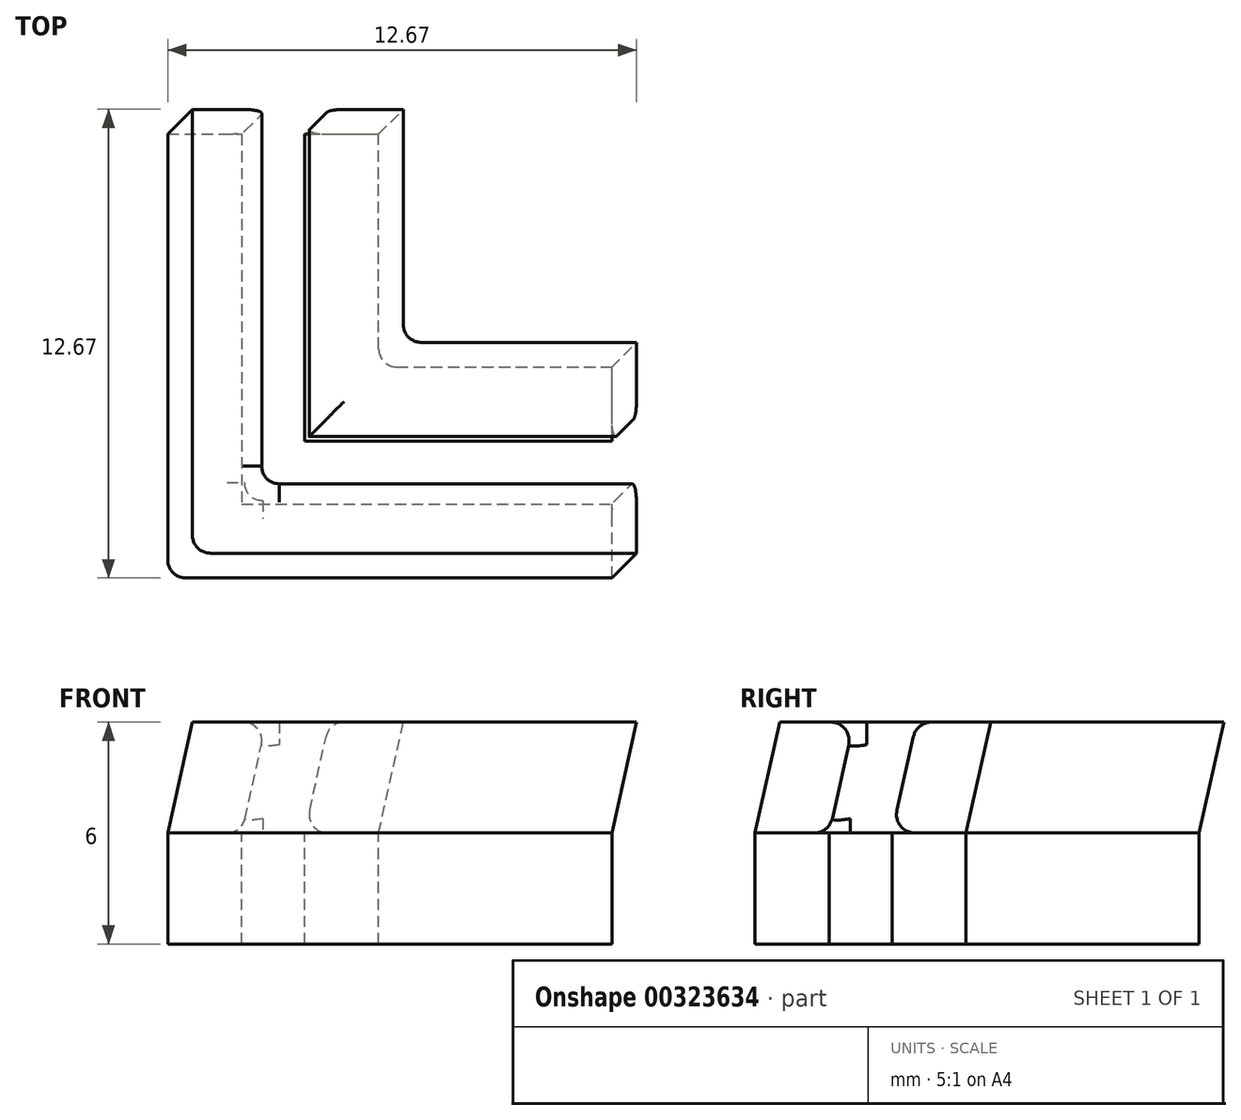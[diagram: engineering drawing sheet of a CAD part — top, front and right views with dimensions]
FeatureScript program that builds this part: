
annotation { "Feature Type Name" : "Feature", "Feature Type Description" : "" }
export const myFeature = defineFeature(function(context is Context, id is Id, definition is map)
    precondition{}
    {
        {
            assignVariable(context, id + "F0", {"name" : "H", "anyValue" : 3});
        }
        {
            var Q0;
            Q0=qCreatedBy(makeId("Top.planeOp"),FACE);
            var sketch = newSketch(context, id + "F1", { "sketchPlane" : qUnion([Q0])});
            skLineSegment(sketch, "E0.bottom", {"start": v(0, 0) * mm, "end": v(12, 0) * mm});
            skLineSegment(sketch, "E0.left", {"start": v(0, 0) * mm, "end": v(0, 12) * mm});
            skLineSegment(sketch, "E0.right", {"start": v(12, 0) * mm, "end": v(12, 5.7) * mm});
            skLineSegment(sketch, "E1.top", {"start": v(0, 12) * mm, "end": v(5.7, 12) * mm});
            skLineSegment(sketch, "E2.bottom", {"start": v(2, 12) * mm, "end": v(3.7, 12) * mm});
            skLineSegment(sketch, "E2.left", {"start": v(2, 12) * mm, "end": v(2, 2) * mm});
            skLineSegment(sketch, "E2.right", {"start": v(3.7, 12) * mm, "end": v(3.7, 3.7) * mm});
            skLineSegment(sketch, "E3.bottom", {"start": v(3.7, 3.7) * mm, "end": v(12, 3.7) * mm});
            skLineSegment(sketch, "E3.top", {"start": v(2, 2) * mm, "end": v(12, 2) * mm});
            skLineSegment(sketch, "E3.right", {"start": v(12, 3.7) * mm, "end": v(12, 2) * mm});
            skLineSegment(sketch, "E4.trimOffspring", {"start": v(5.7, 5.7) * mm, "end": v(12, 5.7) * mm});
            skLineSegment(sketch, "E5.trimOffspring", {"start": v(5.7, 5.7) * mm, "end": v(5.7, 12) * mm});
            skSolve(sketch);
        }
        {
            var Q0;
            {var subQ4=sQuery(id+"F1.wireOp",EDGE,"E0.bottom");Q0=makeQuery(id+"F1.imprint","IMPRINT",FACE,{"disambiguationData":[TD([[makeQuery(id+"F1.imprint","IMPRINT",EDGE,{"derivedFrom":subQ4}),1.0]])]});}
            cPlane(context, id + "F2", {"entities" : qUnion([Q0]), "cplaneType" : CPlaneType.OFFSET, "offset" : (getVariable(context, 'H')) * mm, "width" : 150 * mm, "height" : 150 * mm});
        }
        {
            var Q0;
            Q0=qCreatedBy(id+"F2.planeOp",FACE);
            var sketch = newSketch(context, id + "F3", { "sketchPlane" : qUnion([Q0])});
            skLineSegment(sketch, "E6.bottom", {"start": v(0.67, 0.67) * mm, "end": v(12.67, 0.67) * mm});
            skLineSegment(sketch, "E6.left", {"start": v(0.67, 0.67) * mm, "end": v(0.67, 12.67) * mm});
            skLineSegment(sketch, "E6.right", {"start": v(12.67, 0.67) * mm, "end": v(12.67, 6.37) * mm});
            skLineSegment(sketch, "E7.top", {"start": v(0.67, 12.67) * mm, "end": v(6.37, 12.67) * mm});
            skLineSegment(sketch, "E8.bottom", {"start": v(2.67, 12.67) * mm, "end": v(4.37, 12.67) * mm});
            skLineSegment(sketch, "E8.left", {"start": v(2.67, 12.67) * mm, "end": v(2.67, 2.67) * mm});
            skLineSegment(sketch, "E8.right", {"start": v(4.37, 12.67) * mm, "end": v(4.37, 4.37) * mm});
            skLineSegment(sketch, "E9.bottom", {"start": v(4.37, 4.37) * mm, "end": v(12.67, 4.37) * mm});
            skLineSegment(sketch, "E9.top", {"start": v(2.67, 2.67) * mm, "end": v(12.67, 2.67) * mm});
            skLineSegment(sketch, "E9.right", {"start": v(12.67, 4.37) * mm, "end": v(12.67, 2.67) * mm});
            skLineSegment(sketch, "E10.trimOffspring", {"start": v(6.37, 6.37) * mm, "end": v(12.67, 6.37) * mm});
            skLineSegment(sketch, "E11.trimOffspring", {"start": v(6.37, 6.37) * mm, "end": v(6.37, 12.67) * mm});
            skSolve(sketch);
        }
        {
            var Q0;
            {var subQ4=sQuery(id+"F1.wireOp",EDGE,"E0.bottom");Q0=makeQuery(id+"F1.imprint","IMPRINT",FACE,{"disambiguationData":[TD([[makeQuery(id+"F1.imprint","IMPRINT",EDGE,{"derivedFrom":subQ4}),1.0]])]});}
            var Q1;
            {var subQ4=sQuery(id+"F3.wireOp",EDGE,"E6.bottom");Q1=makeQuery(id+"F3.imprint","IMPRINT",FACE,{"disambiguationData":[TD([[makeQuery(id+"F3.imprint","IMPRINT",EDGE,{"derivedFrom":subQ4}),1.0]])]});}
            loft(context, id + "F4", {"sheetProfilesArray" : [{ "sheetProfileEntities" : qUnion([Q0]) }, { "sheetProfileEntities" : qUnion([Q1]) }]});
        }
        {
            var Q0;
            {var subQ3=sQuery(id+"F1.wireOp",EDGE,"E2.right");Q0=makeQuery(id+"F1.imprint","IMPRINT",FACE,{"disambiguationData":[TD([[makeQuery(id+"F1.imprint","IMPRINT",EDGE,{"derivedFrom":subQ3}),1.0]])]});}
            var Q1;
            {var subQ3=sQuery(id+"F3.wireOp",EDGE,"E8.right");Q1=makeQuery(id+"F3.imprint","IMPRINT",FACE,{"disambiguationData":[TD([[makeQuery(id+"F3.imprint","IMPRINT",EDGE,{"derivedFrom":subQ3}),1.0]])]});}
            loft(context, id + "F5", {"sheetProfilesArray" : [{ "sheetProfileEntities" : qUnion([Q0]) }, { "sheetProfileEntities" : qUnion([Q1]) }]});
        }
        {
            var Q0;
            {var subQ4=sQuery(id+"F1.wireOp",EDGE,"E0.bottom");Q0=makeQuery(id+"F1.imprint","IMPRINT",FACE,{"disambiguationData":[TD([[makeQuery(id+"F1.imprint","IMPRINT",EDGE,{"derivedFrom":subQ4}),1.0]])]});}
            var Q1;
            Q1=makeQuery(id+"F1.imprint","IMPRINT",FACE,{"disambiguationData":[TD([[makeQuery(id+"F1.imprint","IMPRINT",EDGE,{"derivedFrom":sQuery(id+"F1.wireOp",EDGE,"E2.bottom")}),-1.0]])]});
            var Q2;
            {var subQ3=sQuery(id+"F1.wireOp",EDGE,"E2.right");Q2=makeQuery(id+"F1.imprint","IMPRINT",FACE,{"disambiguationData":[TD([[makeQuery(id+"F1.imprint","IMPRINT",EDGE,{"derivedFrom":subQ3}),1.0]])]});}
            extrude(context, id + "F6", {"entities" : qUnion([Q0, Q1, Q2]), "oppositeDirection" : true, "depth" : 3 * mm});
        }
        {
            var Q0;
            Q0=makeQuery(id+"F4.opLoft","MID_CAP_EDGE",EDGE,{"disambiguationData":[OSD([sQuery(id+"F1.wireOp",EDGE,"E0.right"),sQuery(id+"F1.wireOp",EDGE,"E2.left"),sQuery(id+"F1.wireOp",EDGE,"E3.top"),sQuery(id+"F1.wireOp",EDGE,"E3.right")])],"capPos":0.0});
            var Q1;
            Q1=makeQuery(id+"F4.opLoft","MID_CAP_EDGE",EDGE,{"disambiguationData":[OSD([sQuery(id+"F1.wireOp",EDGE,"E1.top"),sQuery(id+"F1.wireOp",EDGE,"E2.bottom"),sQuery(id+"F1.wireOp",EDGE,"E2.left"),sQuery(id+"F1.wireOp",EDGE,"E3.top")])],"capPos":0.0});
            var Q2;
            Q2=makeQuery(id+"F5.opLoft","MID_CAP_EDGE",EDGE,{"disambiguationData":[OSD([sQuery(id+"F1.wireOp",EDGE,"E1.top"),sQuery(id+"F1.wireOp",EDGE,"E2.bottom"),sQuery(id+"F1.wireOp",EDGE,"E2.right"),sQuery(id+"F1.wireOp",EDGE,"E3.bottom")])],"capPos":0.0});
            var Q3;
            Q3=makeQuery(id+"F5.opLoft","MID_CAP_EDGE",EDGE,{"disambiguationData":[OSD([sQuery(id+"F1.wireOp",EDGE,"E0.right"),sQuery(id+"F1.wireOp",EDGE,"E2.right"),sQuery(id+"F1.wireOp",EDGE,"E3.bottom"),sQuery(id+"F1.wireOp",EDGE,"E3.right")])],"capPos":0.0});
            var Q4;
            Q4=makeQuery(id+"F4.opLoft","MID_CAP_EDGE",EDGE,{"disambiguationData":[OSD([sQuery(id+"F3.wireOp",EDGE,"E6.right"),sQuery(id+"F3.wireOp",EDGE,"E8.left"),sQuery(id+"F3.wireOp",EDGE,"E9.top"),sQuery(id+"F3.wireOp",EDGE,"E9.right")])],"capPos":1.0});
            var Q5;
            Q5=makeQuery(id+"F5.opLoft","MID_CAP_EDGE",EDGE,{"disambiguationData":[OSD([sQuery(id+"F3.wireOp",EDGE,"E6.right"),sQuery(id+"F3.wireOp",EDGE,"E8.right"),sQuery(id+"F3.wireOp",EDGE,"E9.bottom"),sQuery(id+"F3.wireOp",EDGE,"E9.right")])],"capPos":1.0});
            var Q6;
            Q6=makeQuery(id+"F5.opLoft","MID_CAP_EDGE",EDGE,{"disambiguationData":[OSD([sQuery(id+"F3.wireOp",EDGE,"E7.top"),sQuery(id+"F3.wireOp",EDGE,"E8.bottom"),sQuery(id+"F3.wireOp",EDGE,"E8.right"),sQuery(id+"F3.wireOp",EDGE,"E9.bottom")])],"capPos":1.0});
            var Q7;
            Q7=makeQuery(id+"F4.opLoft","MID_CAP_EDGE",EDGE,{"disambiguationData":[OSD([sQuery(id+"F3.wireOp",EDGE,"E7.top"),sQuery(id+"F3.wireOp",EDGE,"E8.bottom"),sQuery(id+"F3.wireOp",EDGE,"E8.left"),sQuery(id+"F3.wireOp",EDGE,"E9.top")])],"capPos":1.0});
            var Q8;
            Q8=makeQuery(id+"F4.opLoft","SWEPT_EDGE",EDGE,{"disambiguationData":[OSD([sQuery(id+"F1.wireOp",EDGE,"E2.left"),sQuery(id+"F1.wireOp",EDGE,"E3.top"),sQuery(id+"F3.wireOp",EDGE,"E8.left"),sQuery(id+"F3.wireOp",EDGE,"E9.top")])]});
            var Q9;
            Q9=makeQuery(id+"F6.opExtrude","SWEPT_EDGE",EDGE,{"disambiguationData":[OSD([sQuery(id+"F1.wireOp",EDGE,"E0.bottom"),sQuery(id+"F1.wireOp",EDGE,"E0.left")])]});
            var Q10;
            Q10=makeQuery(id+"F4.opLoft","SWEPT_EDGE",EDGE,{"disambiguationData":[OSD([sQuery(id+"F1.wireOp",EDGE,"E0.bottom"),sQuery(id+"F1.wireOp",EDGE,"E0.left"),sQuery(id+"F3.wireOp",EDGE,"E6.bottom"),sQuery(id+"F3.wireOp",EDGE,"E6.left")])]});
            var Q11;
            Q11=makeQuery(id+"F5.opLoft","SWEPT_EDGE",EDGE,{"disambiguationData":[OSD([sQuery(id+"F1.wireOp",EDGE,"E4.trimOffspring"),sQuery(id+"F1.wireOp",EDGE,"E5.trimOffspring"),sQuery(id+"F3.wireOp",EDGE,"E10.trimOffspring"),sQuery(id+"F3.wireOp",EDGE,"E11.trimOffspring")])]});
            var Q12;
            Q12=makeQuery(id+"F6.opExtrude","SWEPT_EDGE",EDGE,{"disambiguationData":[OSD([sQuery(id+"F1.wireOp",EDGE,"E4.trimOffspring"),sQuery(id+"F1.wireOp",EDGE,"E5.trimOffspring")])]});
            fillet(context, id + "F7", {"entities" : qUnion([Q0, Q1, Q2, Q3, Q4, Q5, Q6, Q7, Q8, Q9, Q10, Q11, Q12]), "radius" : 0.5 * mm, "tangentPropagation" : true, "allowEdgeOverflow" : false});
        }
    });
